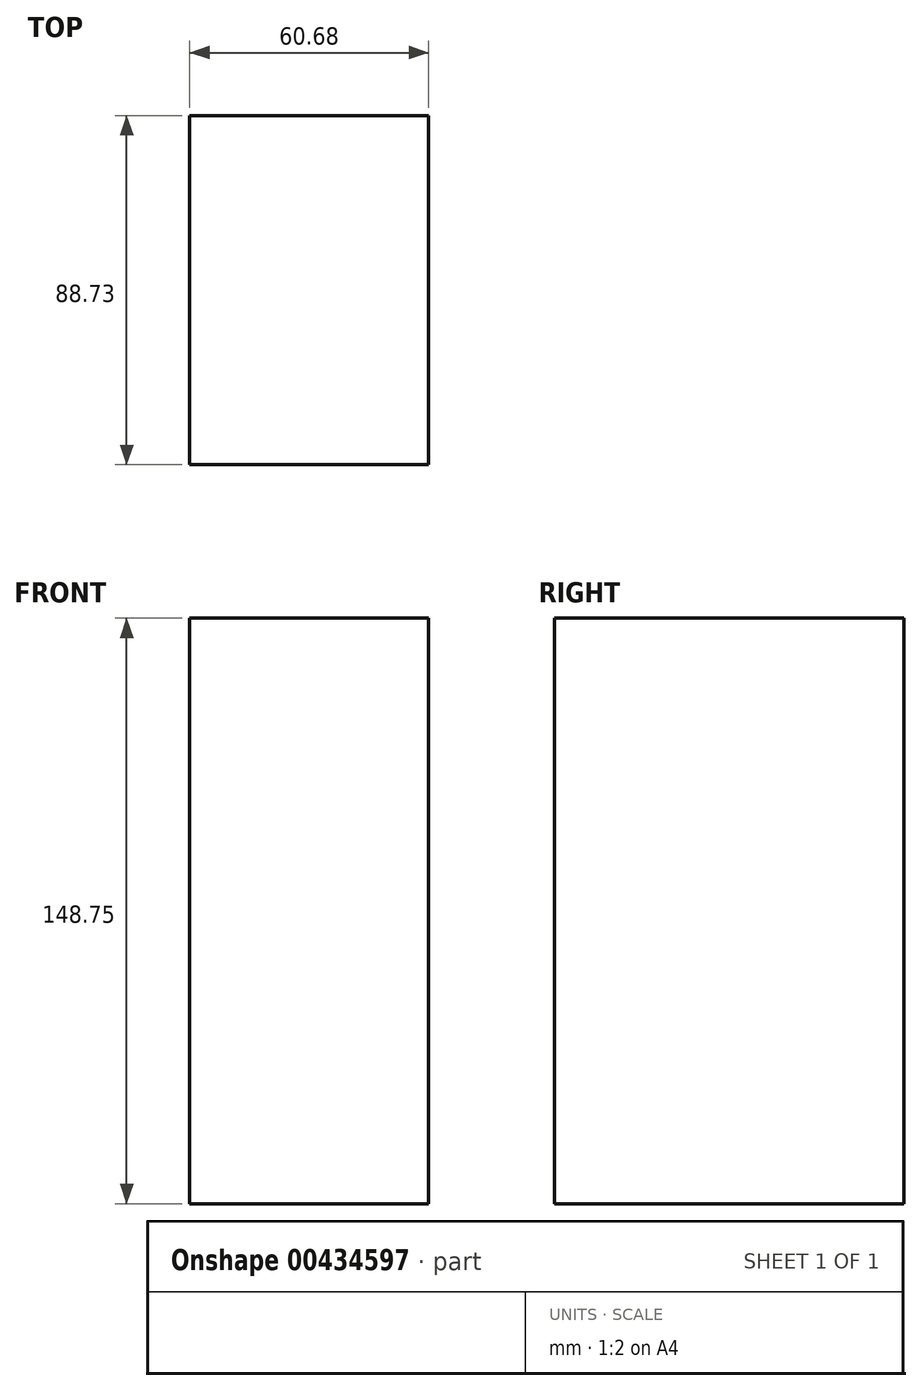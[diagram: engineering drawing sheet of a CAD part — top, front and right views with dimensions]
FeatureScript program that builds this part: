
annotation { "Feature Type Name" : "Feature", "Feature Type Description" : "" }
export const myFeature = defineFeature(function(context is Context, id is Id, definition is map)
    precondition{}
    {
        {
            var Q0;
            Q0=qCreatedBy(makeId("Front.planeOp"),FACE);
            var sketch = newSketch(context, id + "F0", { "sketchPlane" : qUnion([Q0])});
            skLineSegment(sketch, "E0.bottom", {"start": v(0, 0) * mm, "end": v(60.68, 0) * mm});
            skLineSegment(sketch, "E0.top", {"start": v(0, 148.75) * mm, "end": v(60.68, 148.75) * mm});
            skLineSegment(sketch, "E0.left", {"start": v(0, 0) * mm, "end": v(0, 148.75) * mm});
            skLineSegment(sketch, "E0.right", {"start": v(60.68, 0) * mm, "end": v(60.68, 148.75) * mm});
            skSolve(sketch);
        }
        {
            var Q0;
            Q0=makeQuery(id+"F0.imprint","IMPRINT",FACE,{"disambiguationData":[TD([[makeQuery(id+"F0.imprint","IMPRINT",EDGE,{"derivedFrom":sQuery(id+"F0.wireOp",EDGE,"E0.bottom")}),1.0]])]});
            var sketch = newSketch(context, id + "F1", { "sketchPlane" : qUnion([Q0])});
            skSolve(sketch);
        }
        {
            var Q0;
            Q0 = qSketchRegion(id + "F1", true);
            var Q1;
            Q1=makeQuery(id+"F0.imprint","IMPRINT",FACE,{"disambiguationData":[TD([[makeQuery(id+"F0.imprint","IMPRINT",EDGE,{"derivedFrom":sQuery(id+"F0.wireOp",EDGE,"E0.bottom")}),1.0]])]});
            extrude(context, id + "F2", {"entities" : qUnion([Q0, Q1]), "depth" : 88.73 * mm});
        }
    });
